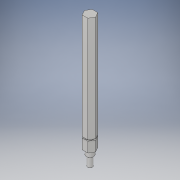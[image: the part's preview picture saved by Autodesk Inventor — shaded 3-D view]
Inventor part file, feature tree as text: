
AUTODESK INVENTOR PART (.ipt)
format: ipt  version: 2019 (Build 230136000, 136)  size: 137,728 bytes
history: native  units: in
note: dims shown in document units (in); Inventor stores cm internally (conversion verified against a paired STEP export)
features: extrude x2, sketch x2, chamfer x1
ambient origin geometry x8: Origin, YZ Plane, XZ Plane, XY Plane, X Axis, Y Axis, Z Axis, Center Point
bodies: Solid1 (feature_tree)
feature tree (5):
  extrude  "Extrusion1"  Depth=5.375in TaperAngle=0.0deg
  extrude  "Extrusion2"  [1 undecoded]
  sketch  "Sketch1"  dims[d0=4.24in d1=0.0in d2=5.375in d3=0.0in]
  sketch  "Sketch2"
  chamfer  "Chamfer1"  [1 undecoded]
note: 2 required parameter values undecoded (feature->parameter linkage not recoverable at this tier; creation-order binding heuristic only, values carry confidence <= 0.55)
